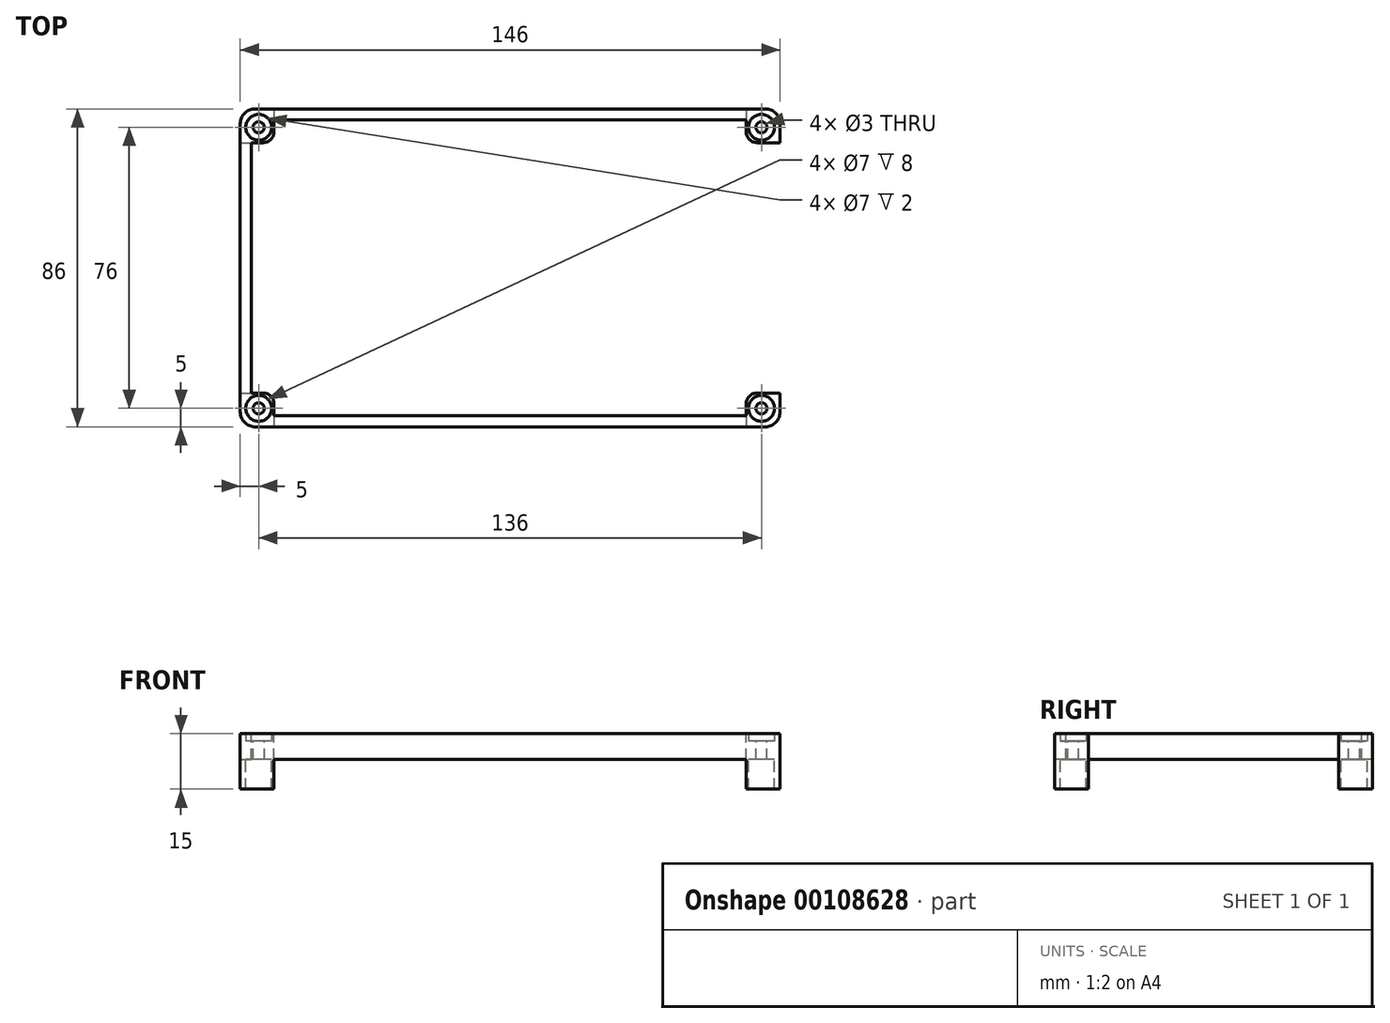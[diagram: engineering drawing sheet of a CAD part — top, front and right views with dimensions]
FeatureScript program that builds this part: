
annotation { "Feature Type Name" : "Feature", "Feature Type Description" : "" }
export const myFeature = defineFeature(function(context is Context, id is Id, definition is map)
    precondition{}
    {
        {
            var Q0;
            Q0=qCreatedBy(makeId("Top.planeOp"),FACE);
            var sketch = newSketch(context, id + "F0", { "sketchPlane" : qUnion([Q0])});
            skLineSegment(sketch, "E0.bottom", {"start": v(4, 0) * mm, "end": v(142, 0) * mm});
            skLineSegment(sketch, "E0.top", {"start": v(4, 86) * mm, "end": v(142, 86) * mm});
            skLineSegment(sketch, "E0.left", {"start": v(0, 4) * mm, "end": v(0, 82) * mm});
            skLineSegment(sketch, "E0.right", {"start": v(146, 4) * mm, "end": v(146, 82) * mm});
            skPoint(sketch, "E1", {"position": v(5, 5) * mm});
            skPoint(sketch, "E2", {"position": v(141, 5) * mm});
            skPoint(sketch, "E3", {"position": v(5, 81) * mm});
            skPoint(sketch, "E4", {"position": v(141, 81) * mm});
            skCircle(sketch, "E5", {"center": v(5, 5) * mm, "radius": 3 * mm, "construction": true});
            skCircle(sketch, "E6", {"center": v(5, 81) * mm, "radius": 3 * mm, "construction": true});
            skCircle(sketch, "E7", {"center": v(141, 81) * mm, "radius": 3 * mm, "construction": true});
            skCircle(sketch, "E8", {"center": v(141, 5) * mm, "radius": 3 * mm, "construction": true});
            skPoint(sketch, "E9", {"position": v(128.5, 7) * mm});
            skPoint(sketch, "E10", {"position": v(118.5, 7) * mm});
            skPoint(sketch, "E11", {"position": v(114.5, 7) * mm});
            skPoint(sketch, "E12", {"position": v(110.5, 7) * mm});
            skPoint(sketch, "E13", {"position": v(17.5, 79) * mm});
            skPoint(sketch, "E14", {"position": v(20.5, 79) * mm});
            skPoint(sketch, "E15", {"position": v(23.5, 79) * mm});
            skPoint(sketch, "E16", {"position": v(26.5, 79) * mm});
            skPoint(sketch, "E17", {"position": v(29.5, 79) * mm});
            skPoint(sketch, "E18", {"position": v(35, 79) * mm});
            skPoint(sketch, "E19", {"position": v(41, 79) * mm});
            skPoint(sketch, "E20", {"position": v(47, 79) * mm});
            skPoint(sketch, "E21", {"position": v(53, 79) * mm});
            skPoint(sketch, "E22", {"position": v(60, 79) * mm});
            skPoint(sketch, "E23", {"position": v(66, 79) * mm});
            skPoint(sketch, "E24", {"position": v(72, 79) * mm});
            skPoint(sketch, "E25", {"position": v(78, 79) * mm});
            skPoint(sketch, "E26", {"position": v(83.5, 79) * mm});
            skPoint(sketch, "E27", {"position": v(146, 10.15) * mm});
            skPoint(sketch, "E28", {"position": v(146, 75.85) * mm});
            skPoint(sketch, "E29", {"position": v(10.15, 0) * mm});
            skPoint(sketch, "E30", {"position": v(135.85, 0) * mm});
            skPoint(sketch, "E31", {"position": v(0, 75.85) * mm});
            skPoint(sketch, "E32", {"position": v(10.15, 86) * mm});
            skPoint(sketch, "E33", {"position": v(0, 10.15) * mm});
            skPoint(sketch, "E34", {"position": v(135.85, 86) * mm});
            skLineSegment(sketch, "E35.bottom", {"start": v(0, 86) * mm, "end": v(10.15, 86) * mm, "construction": true});
            skLineSegment(sketch, "E35.top", {"start": v(0, 75.85) * mm, "end": v(6.15, 75.85) * mm, "construction": true});
            skLineSegment(sketch, "E35.left", {"start": v(0, 86) * mm, "end": v(0, 75.85) * mm, "construction": true});
            skLineSegment(sketch, "E35.right", {"start": v(10.15, 86) * mm, "end": v(10.15, 79.85) * mm, "construction": true});
            skLineSegment(sketch, "E36.bottom", {"start": v(135.85, 86) * mm, "end": v(146, 86) * mm, "construction": true});
            skLineSegment(sketch, "E36.top", {"start": v(139.85, 75.85) * mm, "end": v(146, 75.85) * mm, "construction": true});
            skLineSegment(sketch, "E36.left", {"start": v(135.85, 86) * mm, "end": v(135.85, 79.85) * mm, "construction": true});
            skLineSegment(sketch, "E36.right", {"start": v(146, 86) * mm, "end": v(146, 75.85) * mm, "construction": true});
            skLineSegment(sketch, "E37.bottom", {"start": v(146, 10.15) * mm, "end": v(139.85, 10.15) * mm, "construction": true});
            skLineSegment(sketch, "E37.top", {"start": v(146, 0) * mm, "end": v(135.85, 0) * mm, "construction": true});
            skLineSegment(sketch, "E37.left", {"start": v(146, 10.15) * mm, "end": v(146, 0) * mm, "construction": true});
            skLineSegment(sketch, "E37.right", {"start": v(135.85, 6.15) * mm, "end": v(135.85, 0) * mm, "construction": true});
            skLineSegment(sketch, "E38.bottom", {"start": v(0, 10.15) * mm, "end": v(6.15, 10.15) * mm, "construction": true});
            skLineSegment(sketch, "E38.top", {"start": v(0, 0) * mm, "end": v(10.15, 0) * mm, "construction": true});
            skLineSegment(sketch, "E38.left", {"start": v(0, 10.15) * mm, "end": v(0, 0) * mm, "construction": true});
            skLineSegment(sketch, "E38.right", {"start": v(10.15, 6.15) * mm, "end": v(10.15, 0) * mm, "construction": true});
            skPoint(sketch, "E39.visualSharp", {"position": v(135.85, 75.85) * mm});
            skArc(sketch, "E39.filletArc", {"start": v(135.85, 79.85) * mm, "mid": v(137.02, 77.02) * mm, "end": v(139.85, 75.85) * mm, "construction": true});
            skPoint(sketch, "E40.visualSharp", {"position": v(135.85, 10.15) * mm});
            skArc(sketch, "E40.filletArc", {"start": v(139.85, 10.15) * mm, "mid": v(137.02, 8.98) * mm, "end": v(135.85, 6.15) * mm, "construction": true});
            skPoint(sketch, "E41.visualSharp", {"position": v(10.15, 10.15) * mm});
            skArc(sketch, "E41.filletArc", {"start": v(10.15, 6.15) * mm, "mid": v(8.98, 8.98) * mm, "end": v(6.15, 10.15) * mm, "construction": true});
            skPoint(sketch, "E42.visualSharp", {"position": v(10.15, 75.85) * mm});
            skArc(sketch, "E42.filletArc", {"start": v(6.15, 75.85) * mm, "mid": v(8.98, 77.02) * mm, "end": v(10.15, 79.85) * mm, "construction": true});
            skLineSegment(sketch, "E43.0", {"start": v(3, 83) * mm, "end": v(143, 83) * mm});
            skLineSegment(sketch, "E43.1", {"start": v(3, 3) * mm, "end": v(3, 83) * mm});
            skLineSegment(sketch, "E43.2", {"start": v(3, 3) * mm, "end": v(143, 3) * mm});
            skLineSegment(sketch, "E43.3", {"start": v(143, 3) * mm, "end": v(143, 83) * mm});
            skLineSegment(sketch, "E44.bottom", {"start": v(146, 14.15) * mm, "end": v(143, 14.15) * mm, "construction": true});
            skLineSegment(sketch, "E44.top", {"start": v(146, 20.15) * mm, "end": v(143, 20.15) * mm, "construction": true});
            skLineSegment(sketch, "E44.left", {"start": v(146, 14.15) * mm, "end": v(146, 20.15) * mm});
            skLineSegment(sketch, "E44.right", {"start": v(143, 14.15) * mm, "end": v(143, 20.15) * mm});
            skLineSegment(sketch, "E45.bottom", {"start": v(146, 24.15) * mm, "end": v(143, 24.15) * mm, "construction": true});
            skLineSegment(sketch, "E45.top", {"start": v(146, 30.15) * mm, "end": v(143, 30.15) * mm, "construction": true});
            skLineSegment(sketch, "E45.left", {"start": v(146, 24.15) * mm, "end": v(146, 30.15) * mm});
            skLineSegment(sketch, "E45.right", {"start": v(143, 24.15) * mm, "end": v(143, 30.15) * mm});
            skLineSegment(sketch, "E46.bottom", {"start": v(146, 71.85) * mm, "end": v(143, 71.85) * mm, "construction": true});
            skLineSegment(sketch, "E46.top", {"start": v(146, 65.85) * mm, "end": v(143, 65.85) * mm, "construction": true});
            skLineSegment(sketch, "E46.left", {"start": v(146, 71.85) * mm, "end": v(146, 65.85) * mm});
            skLineSegment(sketch, "E46.right", {"start": v(143, 71.85) * mm, "end": v(143, 65.85) * mm});
            skLineSegment(sketch, "E47.bottom", {"start": v(146, 61.85) * mm, "end": v(143, 61.85) * mm, "construction": true});
            skLineSegment(sketch, "E47.top", {"start": v(146, 55.85) * mm, "end": v(143, 55.85) * mm, "construction": true});
            skLineSegment(sketch, "E47.left", {"start": v(146, 61.85) * mm, "end": v(146, 55.85) * mm});
            skLineSegment(sketch, "E47.right", {"start": v(143, 61.85) * mm, "end": v(143, 55.85) * mm});
            skLineSegment(sketch, "E48.bottom", {"start": v(146, 51.85) * mm, "end": v(143, 51.85) * mm, "construction": true});
            skLineSegment(sketch, "E48.top", {"start": v(146, 45.85) * mm, "end": v(143, 45.85) * mm, "construction": true});
            skLineSegment(sketch, "E48.left", {"start": v(146, 51.85) * mm, "end": v(146, 45.85) * mm});
            skLineSegment(sketch, "E48.right", {"start": v(143, 51.85) * mm, "end": v(143, 45.85) * mm});
            skLineSegment(sketch, "E49.bottom", {"start": v(146, 41.85) * mm, "end": v(143, 41.85) * mm, "construction": true});
            skLineSegment(sketch, "E49.top", {"start": v(146, 35.85) * mm, "end": v(143, 35.85) * mm, "construction": true});
            skLineSegment(sketch, "E49.left", {"start": v(146, 41.85) * mm, "end": v(146, 35.85) * mm});
            skLineSegment(sketch, "E49.right", {"start": v(143, 41.85) * mm, "end": v(143, 35.85) * mm});
            skLineSegment(sketch, "E50.0", {"start": v(9.15, 6.15) * mm, "end": v(9.15, 0) * mm});
            skArc(sketch, "E50.1", {"start": v(9.15, 6.15) * mm, "mid": v(8.27, 8.27) * mm, "end": v(6.15, 9.15) * mm});
            skLineSegment(sketch, "E50.2", {"start": v(0, 9.15) * mm, "end": v(6.15, 9.15) * mm});
            skLineSegment(sketch, "E51.0", {"start": v(136.85, 6.15) * mm, "end": v(136.85, 0) * mm});
            skArc(sketch, "E51.1", {"start": v(139.85, 9.15) * mm, "mid": v(137.73, 8.27) * mm, "end": v(136.85, 6.15) * mm});
            skLineSegment(sketch, "E51.2", {"start": v(146, 9.15) * mm, "end": v(139.85, 9.15) * mm});
            skLineSegment(sketch, "E52.0", {"start": v(139.85, 76.85) * mm, "end": v(146, 76.85) * mm});
            skArc(sketch, "E52.1", {"start": v(136.85, 79.85) * mm, "mid": v(137.73, 77.73) * mm, "end": v(139.85, 76.85) * mm});
            skLineSegment(sketch, "E52.2", {"start": v(136.85, 86) * mm, "end": v(136.85, 79.85) * mm});
            skLineSegment(sketch, "E53.0", {"start": v(9.15, 86) * mm, "end": v(9.15, 79.85) * mm});
            skArc(sketch, "E53.1", {"start": v(6.15, 76.85) * mm, "mid": v(8.27, 77.73) * mm, "end": v(9.15, 79.85) * mm});
            skLineSegment(sketch, "E53.2", {"start": v(0, 76.85) * mm, "end": v(6.15, 76.85) * mm});
            skCircle(sketch, "E54.0", {"center": v(5, 5) * mm, "radius": 3.5 * mm});
            skCircle(sketch, "E55.0", {"center": v(141, 5) * mm, "radius": 3.5 * mm});
            skCircle(sketch, "E56.0", {"center": v(141, 81) * mm, "radius": 3.5 * mm});
            skCircle(sketch, "E57.0", {"center": v(5, 81) * mm, "radius": 3.5 * mm});
            skLineSegment(sketch, "E58.bottom", {"start": v(0, 14.15) * mm, "end": v(3, 14.15) * mm});
            skLineSegment(sketch, "E58.top", {"start": v(0, 20.15) * mm, "end": v(3, 20.15) * mm});
            skLineSegment(sketch, "E58.left", {"start": v(0, 14.15) * mm, "end": v(0, 20.15) * mm});
            skLineSegment(sketch, "E58.right", {"start": v(3, 14.15) * mm, "end": v(3, 20.15) * mm});
            skLineSegment(sketch, "E59.bottom", {"start": v(0, 24.15) * mm, "end": v(3, 24.15) * mm});
            skLineSegment(sketch, "E59.top", {"start": v(0, 30.15) * mm, "end": v(3, 30.15) * mm});
            skLineSegment(sketch, "E59.left", {"start": v(0, 24.15) * mm, "end": v(0, 30.15) * mm});
            skLineSegment(sketch, "E59.right", {"start": v(3, 24.15) * mm, "end": v(3, 30.15) * mm});
            skLineSegment(sketch, "E60.bottom", {"start": v(0, 35.85) * mm, "end": v(3, 35.85) * mm});
            skLineSegment(sketch, "E60.top", {"start": v(0, 41.85) * mm, "end": v(3, 41.85) * mm});
            skLineSegment(sketch, "E60.left", {"start": v(0, 35.85) * mm, "end": v(0, 41.85) * mm});
            skLineSegment(sketch, "E60.right", {"start": v(3, 35.85) * mm, "end": v(3, 41.85) * mm});
            skLineSegment(sketch, "E61.bottom", {"start": v(0, 45.85) * mm, "end": v(3, 45.85) * mm});
            skLineSegment(sketch, "E61.top", {"start": v(0, 51.85) * mm, "end": v(3, 51.85) * mm});
            skLineSegment(sketch, "E61.left", {"start": v(0, 45.85) * mm, "end": v(0, 51.85) * mm});
            skLineSegment(sketch, "E61.right", {"start": v(3, 45.85) * mm, "end": v(3, 51.85) * mm});
            skLineSegment(sketch, "E62.bottom", {"start": v(0, 55.85) * mm, "end": v(3, 55.85) * mm});
            skLineSegment(sketch, "E62.top", {"start": v(0, 61.85) * mm, "end": v(3, 61.85) * mm});
            skLineSegment(sketch, "E62.left", {"start": v(0, 55.85) * mm, "end": v(0, 61.85) * mm});
            skLineSegment(sketch, "E62.right", {"start": v(3, 55.85) * mm, "end": v(3, 61.85) * mm});
            skLineSegment(sketch, "E63.bottom", {"start": v(0, 65.85) * mm, "end": v(3, 65.85) * mm});
            skLineSegment(sketch, "E63.top", {"start": v(0, 71.85) * mm, "end": v(3, 71.85) * mm});
            skLineSegment(sketch, "E63.left", {"start": v(0, 65.85) * mm, "end": v(0, 71.85) * mm});
            skLineSegment(sketch, "E63.right", {"start": v(3, 65.85) * mm, "end": v(3, 71.85) * mm});
            skCircle(sketch, "E64", {"center": v(5, 5) * mm, "radius": 1.5 * mm});
            skCircle(sketch, "E65", {"center": v(5, 81) * mm, "radius": 1.5 * mm});
            skCircle(sketch, "E66", {"center": v(141, 81) * mm, "radius": 1.5 * mm});
            skCircle(sketch, "E67", {"center": v(141, 5) * mm, "radius": 1.5 * mm});
            skPoint(sketch, "E68.visualSharp", {"position": v(0, 0) * mm});
            skArc(sketch, "E68.filletArc", {"start": v(0, 4) * mm, "mid": v(1.17, 1.17) * mm, "end": v(4, 0) * mm});
            skPoint(sketch, "E69.visualSharp", {"position": v(146, 86) * mm});
            skArc(sketch, "E69.filletArc", {"start": v(146, 82) * mm, "mid": v(144.83, 84.83) * mm, "end": v(142, 86) * mm});
            skPoint(sketch, "E70.visualSharp", {"position": v(146, 0) * mm});
            skArc(sketch, "E70.filletArc", {"start": v(142, 0) * mm, "mid": v(144.83, 1.17) * mm, "end": v(146, 4) * mm});
            skPoint(sketch, "E71.visualSharp", {"position": v(0, 86) * mm});
            skArc(sketch, "E71.filletArc", {"start": v(4, 86) * mm, "mid": v(1.17, 84.83) * mm, "end": v(0, 82) * mm});
            skSolve(sketch);
        }
        {
            var Q0;
            {var subQ1=sQuery(id+"F0.wireOp",EDGE,"E38.top");Q0=makeQuery(id+"F0.imprint","IMPRINT",FACE,{"disambiguationData":[TD([[makeQuery(id+"F0.imprint","IMPRINT",EDGE,{"derivedFrom":subQ1}),1.0]])]});}
            var Q1;
            {var subQ0=sQuery(id+"F0.wireOp",EDGE,"E0.bottom");Q1=makeQuery(id+"F0.imprint","IMPRINT",FACE,{"disambiguationData":[TD([[makeQuery(id+"F0.imprint","IMPRINT",EDGE,{"derivedFrom":subQ0}),1.0]])]});}
            var Q2;
            {var subQ0=sQuery(id+"F0.wireOp",EDGE,"E0.left");Q2=makeQuery(id+"F0.imprint","IMPRINT",FACE,{"disambiguationData":[TD([[makeQuery(id+"F0.imprint","IMPRINT",EDGE,{"derivedFrom":subQ0}),-1.0]])]});}
            var Q3;
            {var subQ0=sQuery(id+"F0.wireOp",EDGE,"E41.filletArc");Q3=makeQuery(id+"F0.imprint","IMPRINT",FACE,{"disambiguationData":[TD([[makeQuery(id+"F0.imprint","IMPRINT",EDGE,{"derivedFrom":subQ0}),1.0]])]});}
            var Q4;
            {var subQ4=sQuery(id+"F0.wireOp",EDGE,"E35.bottom");Q4=makeQuery(id+"F0.imprint","IMPRINT",FACE,{"disambiguationData":[TD([[makeQuery(id+"F0.imprint","IMPRINT",EDGE,{"derivedFrom":subQ4}),-1.0]])]});}
            var Q5;
            {var subQ0=sQuery(id+"F0.wireOp",EDGE,"E42.filletArc");Q5=makeQuery(id+"F0.imprint","IMPRINT",FACE,{"disambiguationData":[TD([[makeQuery(id+"F0.imprint","IMPRINT",EDGE,{"derivedFrom":subQ0}),1.0]])]});}
            var Q6;
            {var subQ0=sQuery(id+"F0.wireOp",EDGE,"E0.top");Q6=makeQuery(id+"F0.imprint","IMPRINT",FACE,{"disambiguationData":[TD([[makeQuery(id+"F0.imprint","IMPRINT",EDGE,{"derivedFrom":subQ0}),-1.0]])]});}
            var Q7;
            {var subQ1=sQuery(id+"F0.wireOp",EDGE,"E36.bottom");Q7=makeQuery(id+"F0.imprint","IMPRINT",FACE,{"disambiguationData":[TD([[makeQuery(id+"F0.imprint","IMPRINT",EDGE,{"derivedFrom":subQ1}),-1.0]])]});}
            var Q8;
            {var subQ0=sQuery(id+"F0.wireOp",EDGE,"E39.filletArc");Q8=makeQuery(id+"F0.imprint","IMPRINT",FACE,{"disambiguationData":[TD([[makeQuery(id+"F0.imprint","IMPRINT",EDGE,{"derivedFrom":subQ0}),1.0]])]});}
            var Q9;
            {var subQ1=sQuery(id+"F0.wireOp",EDGE,"E37.top");Q9=makeQuery(id+"F0.imprint","IMPRINT",FACE,{"disambiguationData":[TD([[makeQuery(id+"F0.imprint","IMPRINT",EDGE,{"derivedFrom":subQ1}),-1.0]])]});}
            var Q10;
            {var subQ0=sQuery(id+"F0.wireOp",EDGE,"E40.filletArc");Q10=makeQuery(id+"F0.imprint","IMPRINT",FACE,{"disambiguationData":[TD([[makeQuery(id+"F0.imprint","IMPRINT",EDGE,{"derivedFrom":subQ0}),1.0]])]});}
            var Q11;
            {var subQ3=sQuery(id+"F0.wireOp",EDGE,"E44.bottom");Q11=makeQuery(id+"F0.imprint","IMPRINT",FACE,{"disambiguationData":[TD([[makeQuery(id+"F0.imprint","IMPRINT",EDGE,{"derivedFrom":subQ3}),1.0]])]});}
            var Q12;
            Q12=makeQuery(id+"F0.imprint","IMPRINT",FACE,{"disambiguationData":[TD([[makeQuery(id+"F0.imprint","IMPRINT",EDGE,{"derivedFrom":sQuery(id+"F0.wireOp",EDGE,"E44.bottom")}),-1.0]])]});
            var Q13;
            {var subQ0=sQuery(id+"F0.wireOp",EDGE,"E44.top");Q13=makeQuery(id+"F0.imprint","IMPRINT",FACE,{"disambiguationData":[TD([[makeQuery(id+"F0.imprint","IMPRINT",EDGE,{"derivedFrom":subQ0}),-1.0]])]});}
            var Q14;
            Q14=makeQuery(id+"F0.imprint","IMPRINT",FACE,{"disambiguationData":[TD([[makeQuery(id+"F0.imprint","IMPRINT",EDGE,{"derivedFrom":sQuery(id+"F0.wireOp",EDGE,"E45.bottom")}),-1.0]])]});
            var Q15;
            {var subQ0=sQuery(id+"F0.wireOp",EDGE,"E45.top");Q15=makeQuery(id+"F0.imprint","IMPRINT",FACE,{"disambiguationData":[TD([[makeQuery(id+"F0.imprint","IMPRINT",EDGE,{"derivedFrom":subQ0}),-1.0]])]});}
            var Q16;
            Q16=makeQuery(id+"F0.imprint","IMPRINT",FACE,{"disambiguationData":[TD([[makeQuery(id+"F0.imprint","IMPRINT",EDGE,{"derivedFrom":sQuery(id+"F0.wireOp",EDGE,"E49.bottom")}),1.0]])]});
            var Q17;
            {var subQ0=sQuery(id+"F0.wireOp",EDGE,"E48.top");Q17=makeQuery(id+"F0.imprint","IMPRINT",FACE,{"disambiguationData":[TD([[makeQuery(id+"F0.imprint","IMPRINT",EDGE,{"derivedFrom":subQ0}),1.0]])]});}
            var Q18;
            Q18=makeQuery(id+"F0.imprint","IMPRINT",FACE,{"disambiguationData":[TD([[makeQuery(id+"F0.imprint","IMPRINT",EDGE,{"derivedFrom":sQuery(id+"F0.wireOp",EDGE,"E48.bottom")}),1.0]])]});
            var Q19;
            {var subQ0=sQuery(id+"F0.wireOp",EDGE,"E47.top");Q19=makeQuery(id+"F0.imprint","IMPRINT",FACE,{"disambiguationData":[TD([[makeQuery(id+"F0.imprint","IMPRINT",EDGE,{"derivedFrom":subQ0}),1.0]])]});}
            var Q20;
            Q20=makeQuery(id+"F0.imprint","IMPRINT",FACE,{"disambiguationData":[TD([[makeQuery(id+"F0.imprint","IMPRINT",EDGE,{"derivedFrom":sQuery(id+"F0.wireOp",EDGE,"E47.bottom")}),1.0]])]});
            var Q21;
            {var subQ0=sQuery(id+"F0.wireOp",EDGE,"E46.top");Q21=makeQuery(id+"F0.imprint","IMPRINT",FACE,{"disambiguationData":[TD([[makeQuery(id+"F0.imprint","IMPRINT",EDGE,{"derivedFrom":subQ0}),1.0]])]});}
            var Q22;
            Q22=makeQuery(id+"F0.imprint","IMPRINT",FACE,{"disambiguationData":[TD([[makeQuery(id+"F0.imprint","IMPRINT",EDGE,{"derivedFrom":sQuery(id+"F0.wireOp",EDGE,"E46.bottom")}),1.0]])]});
            var Q23;
            {var subQ3=sQuery(id+"F0.wireOp",EDGE,"E46.bottom");Q23=makeQuery(id+"F0.imprint","IMPRINT",FACE,{"disambiguationData":[TD([[makeQuery(id+"F0.imprint","IMPRINT",EDGE,{"derivedFrom":subQ3}),-1.0]])]});}
            var Q24;
            {var subQ0=sQuery(id+"F0.wireOp",EDGE,"E43.1");var subQ1=sQuery(id+"F0.wireOp",EDGE,"E5");var subQ2=makeQuery(id+"F0.imprint","INTERSECT",VERTEX,{"derivedFrom":[subQ1,subQ0]});Q24=makeQuery(id+"F0.imprint","IMPRINT",FACE,{"disambiguationData":[TD([[makeQuery(id+"F0.imprint","IMPRINT",EDGE,{"disambiguationData":[TD([[subQ2,-1.0]])],"derivedFrom":subQ1}),-1.0]])]});}
            var Q25;
            {var subQ0=sQuery(id+"F0.wireOp",EDGE,"E50.1");Q25=makeQuery(id+"F0.imprint","IMPRINT",FACE,{"disambiguationData":[TD([[makeQuery(id+"F0.imprint","IMPRINT",EDGE,{"derivedFrom":subQ0}),1.0]])]});}
            var Q26;
            {var subQ0=sQuery(id+"F0.wireOp",EDGE,"E43.0");var subQ1=sQuery(id+"F0.wireOp",EDGE,"E6");var subQ2=makeQuery(id+"F0.imprint","INTERSECT",VERTEX,{"derivedFrom":[subQ1,subQ0]});Q26=makeQuery(id+"F0.imprint","IMPRINT",FACE,{"disambiguationData":[TD([[makeQuery(id+"F0.imprint","IMPRINT",EDGE,{"disambiguationData":[TD([[subQ2,-1.0]])],"derivedFrom":subQ1}),-1.0]])]});}
            var Q27;
            {var subQ0=sQuery(id+"F0.wireOp",EDGE,"E53.1");Q27=makeQuery(id+"F0.imprint","IMPRINT",FACE,{"disambiguationData":[TD([[makeQuery(id+"F0.imprint","IMPRINT",EDGE,{"derivedFrom":subQ0}),1.0]])]});}
            var Q28;
            {var subQ0=sQuery(id+"F0.wireOp",EDGE,"E43.0");var subQ1=sQuery(id+"F0.wireOp",EDGE,"E7");var subQ2=makeQuery(id+"F0.imprint","INTERSECT",VERTEX,{"derivedFrom":[subQ1,subQ0]});Q28=makeQuery(id+"F0.imprint","IMPRINT",FACE,{"disambiguationData":[TD([[makeQuery(id+"F0.imprint","IMPRINT",EDGE,{"disambiguationData":[TD([[subQ2,1.0]])],"derivedFrom":subQ1}),-1.0]])]});}
            var Q29;
            {var subQ5=sQuery(id+"F0.wireOp",EDGE,"E52.1");Q29=makeQuery(id+"F0.imprint","IMPRINT",FACE,{"disambiguationData":[TD([[makeQuery(id+"F0.imprint","IMPRINT",EDGE,{"derivedFrom":subQ5}),1.0]])]});}
            var Q30;
            {var subQ0=sQuery(id+"F0.wireOp",EDGE,"E43.2");var subQ1=sQuery(id+"F0.wireOp",EDGE,"E8");var subQ2=makeQuery(id+"F0.imprint","INTERSECT",VERTEX,{"derivedFrom":[subQ1,subQ0]});Q30=makeQuery(id+"F0.imprint","IMPRINT",FACE,{"disambiguationData":[TD([[makeQuery(id+"F0.imprint","IMPRINT",EDGE,{"disambiguationData":[TD([[subQ2,-1.0]])],"derivedFrom":subQ1}),-1.0]])]});}
            var Q31;
            {var subQ0=sQuery(id+"F0.wireOp",EDGE,"E51.1");Q31=makeQuery(id+"F0.imprint","IMPRINT",FACE,{"disambiguationData":[TD([[makeQuery(id+"F0.imprint","IMPRINT",EDGE,{"derivedFrom":subQ0}),1.0]])]});}
            var Q32;
            {var subQ6=sQuery(id+"F0.wireOp",EDGE,"E38.left");var subQ11=sQuery(id+"F0.wireOp",EDGE,"E38.top");var subQ13=makeQuery(id+"F0.imprint","INTERSECT",VERTEX,{"derivedFrom":[subQ11,subQ6]});Q32=makeQuery(id+"F0.imprint","IMPRINT",FACE,{"disambiguationData":[TD([[makeQuery(id+"F0.imprint","IMPRINT",EDGE,{"disambiguationData":[TD([[subQ13,-1.0]])],"derivedFrom":subQ11}),1.0]])]});}
            var Q33;
            {var subQ5=sQuery(id+"F0.wireOp",EDGE,"E37.left");var subQ6=sQuery(id+"F0.wireOp",EDGE,"E37.top");var subQ7=makeQuery(id+"F0.imprint","INTERSECT",VERTEX,{"derivedFrom":[subQ6,subQ5]});Q33=makeQuery(id+"F0.imprint","IMPRINT",FACE,{"disambiguationData":[TD([[makeQuery(id+"F0.imprint","IMPRINT",EDGE,{"disambiguationData":[TD([[subQ7,-1.0]])],"derivedFrom":subQ6}),-1.0]])]});}
            var Q34;
            {var subQ5=sQuery(id+"F0.wireOp",EDGE,"E36.right");var subQ6=sQuery(id+"F0.wireOp",EDGE,"E36.bottom");var subQ7=makeQuery(id+"F0.imprint","INTERSECT",VERTEX,{"derivedFrom":[subQ6,subQ5]});Q34=makeQuery(id+"F0.imprint","IMPRINT",FACE,{"disambiguationData":[TD([[makeQuery(id+"F0.imprint","IMPRINT",EDGE,{"disambiguationData":[TD([[subQ7,1.0]])],"derivedFrom":subQ6}),-1.0]])]});}
            var Q35;
            {var subQ9=sQuery(id+"F0.wireOp",EDGE,"E35.left");var subQ10=sQuery(id+"F0.wireOp",EDGE,"E35.bottom");var subQ11=makeQuery(id+"F0.imprint","INTERSECT",VERTEX,{"derivedFrom":[subQ10,subQ9]});Q35=makeQuery(id+"F0.imprint","IMPRINT",FACE,{"disambiguationData":[TD([[makeQuery(id+"F0.imprint","IMPRINT",EDGE,{"disambiguationData":[TD([[subQ11,-1.0]])],"derivedFrom":subQ10}),-1.0]])]});}
            var Q36;
            {var subQ5=sQuery(id+"F0.wireOp",EDGE,"E58.bottom");Q36=makeQuery(id+"F0.imprint","IMPRINT",FACE,{"disambiguationData":[TD([[makeQuery(id+"F0.imprint","IMPRINT",EDGE,{"derivedFrom":subQ5}),-1.0]])]});}
            var Q37;
            Q37=makeQuery(id+"F0.imprint","IMPRINT",FACE,{"disambiguationData":[TD([[makeQuery(id+"F0.imprint","IMPRINT",EDGE,{"derivedFrom":sQuery(id+"F0.wireOp",EDGE,"E58.bottom")}),1.0]])]});
            var Q38;
            Q38=makeQuery(id+"F0.imprint","IMPRINT",FACE,{"disambiguationData":[TD([[makeQuery(id+"F0.imprint","IMPRINT",EDGE,{"derivedFrom":sQuery(id+"F0.wireOp",EDGE,"E59.bottom")}),1.0]])]});
            var Q39;
            Q39=makeQuery(id+"F0.imprint","IMPRINT",FACE,{"disambiguationData":[TD([[makeQuery(id+"F0.imprint","IMPRINT",EDGE,{"derivedFrom":sQuery(id+"F0.wireOp",EDGE,"E60.bottom")}),1.0]])]});
            var Q40;
            Q40=makeQuery(id+"F0.imprint","IMPRINT",FACE,{"disambiguationData":[TD([[makeQuery(id+"F0.imprint","IMPRINT",EDGE,{"derivedFrom":sQuery(id+"F0.wireOp",EDGE,"E61.bottom")}),1.0]])]});
            var Q41;
            Q41=makeQuery(id+"F0.imprint","IMPRINT",FACE,{"disambiguationData":[TD([[makeQuery(id+"F0.imprint","IMPRINT",EDGE,{"derivedFrom":sQuery(id+"F0.wireOp",EDGE,"E62.bottom")}),1.0]])]});
            var Q42;
            Q42=makeQuery(id+"F0.imprint","IMPRINT",FACE,{"disambiguationData":[TD([[makeQuery(id+"F0.imprint","IMPRINT",EDGE,{"derivedFrom":sQuery(id+"F0.wireOp",EDGE,"E63.bottom")}),1.0]])]});
            var Q43;
            {var subQ0=sQuery(id+"F0.wireOp",EDGE,"E63.top");Q43=makeQuery(id+"F0.imprint","IMPRINT",FACE,{"disambiguationData":[TD([[makeQuery(id+"F0.imprint","IMPRINT",EDGE,{"derivedFrom":subQ0}),1.0]])]});}
            var Q44;
            {var subQ4=sQuery(id+"F0.wireOp",EDGE,"E44.left");Q44=makeQuery(id+"F0.imprint","IMPRINT",FACE,{"disambiguationData":[TD([[makeQuery(id+"F0.imprint","IMPRINT",EDGE,{"derivedFrom":subQ4}),1.0]])]});}
            var Q45;
            {var subQ0=sQuery(id+"F0.wireOp",EDGE,"E43.2");var subQ1=sQuery(id+"F0.wireOp",EDGE,"E43.1");var subQ2=makeQuery(id+"F0.imprint","INTERSECT",VERTEX,{"derivedFrom":[subQ1,subQ0]});Q45=makeQuery(id+"F0.imprint","IMPRINT",FACE,{"disambiguationData":[TD([[makeQuery(id+"F0.imprint","IMPRINT",EDGE,{"disambiguationData":[TD([[subQ2,-1.0]])],"derivedFrom":subQ1}),1.0]])]});}
            var Q46;
            Q46=makeQuery(id+"F0.imprint","IMPRINT",FACE,{"disambiguationData":[TD([[makeQuery(id+"F0.imprint","IMPRINT",EDGE,{"derivedFrom":sQuery(id+"F0.wireOp",EDGE,"E64")}),-1.0]])]});
            var Q47;
            {var subQ0=sQuery(id+"F0.wireOp",EDGE,"E43.1");var subQ1=sQuery(id+"F0.wireOp",EDGE,"E43.0");var subQ2=makeQuery(id+"F0.imprint","INTERSECT",VERTEX,{"derivedFrom":[subQ1,subQ0]});Q47=makeQuery(id+"F0.imprint","IMPRINT",FACE,{"disambiguationData":[TD([[makeQuery(id+"F0.imprint","IMPRINT",EDGE,{"disambiguationData":[TD([[subQ2,-1.0]])],"derivedFrom":subQ1}),1.0]])]});}
            var Q48;
            Q48=makeQuery(id+"F0.imprint","IMPRINT",FACE,{"disambiguationData":[TD([[makeQuery(id+"F0.imprint","IMPRINT",EDGE,{"derivedFrom":sQuery(id+"F0.wireOp",EDGE,"E65")}),-1.0]])]});
            var Q49;
            {var subQ0=sQuery(id+"F0.wireOp",EDGE,"E43.3");var subQ1=sQuery(id+"F0.wireOp",EDGE,"E43.0");var subQ2=makeQuery(id+"F0.imprint","INTERSECT",VERTEX,{"derivedFrom":[subQ1,subQ0]});Q49=makeQuery(id+"F0.imprint","IMPRINT",FACE,{"disambiguationData":[TD([[makeQuery(id+"F0.imprint","IMPRINT",EDGE,{"disambiguationData":[TD([[subQ2,1.0]])],"derivedFrom":subQ1}),1.0]])]});}
            var Q50;
            Q50=makeQuery(id+"F0.imprint","IMPRINT",FACE,{"disambiguationData":[TD([[makeQuery(id+"F0.imprint","IMPRINT",EDGE,{"derivedFrom":sQuery(id+"F0.wireOp",EDGE,"E66")}),-1.0]])]});
            var Q51;
            Q51=makeQuery(id+"F0.imprint","IMPRINT",FACE,{"disambiguationData":[TD([[makeQuery(id+"F0.imprint","IMPRINT",EDGE,{"derivedFrom":sQuery(id+"F0.wireOp",EDGE,"E67")}),-1.0]])]});
            var Q52;
            {var subQ0=sQuery(id+"F0.wireOp",EDGE,"E43.3");var subQ1=sQuery(id+"F0.wireOp",EDGE,"E43.2");var subQ2=makeQuery(id+"F0.imprint","INTERSECT",VERTEX,{"derivedFrom":[subQ1,subQ0]});Q52=makeQuery(id+"F0.imprint","IMPRINT",FACE,{"disambiguationData":[TD([[makeQuery(id+"F0.imprint","IMPRINT",EDGE,{"disambiguationData":[TD([[subQ2,1.0]])],"derivedFrom":subQ1}),-1.0]])]});}
            var Q53;
            {var subQ11=sQuery(id+"F0.wireOp",EDGE,"E68.filletArc");Q53=makeQuery(id+"F0.imprint","IMPRINT",FACE,{"disambiguationData":[TD([[makeQuery(id+"F0.imprint","IMPRINT",EDGE,{"derivedFrom":subQ11}),1.0]])]});}
            var Q54;
            {var subQ5=sQuery(id+"F0.wireOp",EDGE,"E71.filletArc");Q54=makeQuery(id+"F0.imprint","IMPRINT",FACE,{"disambiguationData":[TD([[makeQuery(id+"F0.imprint","IMPRINT",EDGE,{"derivedFrom":subQ5}),1.0]])]});}
            var Q55;
            {var subQ9=sQuery(id+"F0.wireOp",EDGE,"E69.filletArc");Q55=makeQuery(id+"F0.imprint","IMPRINT",FACE,{"disambiguationData":[TD([[makeQuery(id+"F0.imprint","IMPRINT",EDGE,{"derivedFrom":subQ9}),1.0]])]});}
            var Q56;
            {var subQ9=sQuery(id+"F0.wireOp",EDGE,"E70.filletArc");Q56=makeQuery(id+"F0.imprint","IMPRINT",FACE,{"disambiguationData":[TD([[makeQuery(id+"F0.imprint","IMPRINT",EDGE,{"derivedFrom":subQ9}),1.0]])]});}
            extrude(context, id + "F1", {"entities" : qUnion([Q0, Q1, Q2, Q3, Q4, Q5, Q6, Q7, Q8, Q9, Q10, Q11, Q12, Q13, Q14, Q15, Q16, Q17, Q18, Q19, Q20, Q21, Q22, Q23, Q24, Q25, Q26, Q27, Q28, Q29, Q30, Q31, Q32, Q33, Q34, Q35, Q36, Q37, Q38, Q39, Q40, Q41, Q42, Q43, Q44, Q45, Q46, Q47, Q48, Q49, Q50, Q51, Q52, Q53, Q54, Q55, Q56]), "oppositeDirection" : true, "depth" : 2.5 * mm});
        }
        {
            var Q0;
            {var subQ0=sQuery(id+"F0.wireOp",EDGE,"E0.bottom");Q0=makeQuery(id+"F0.imprint","IMPRINT",FACE,{"disambiguationData":[TD([[makeQuery(id+"F0.imprint","IMPRINT",EDGE,{"derivedFrom":subQ0}),1.0]])]});}
            var Q1;
            {var subQ0=sQuery(id+"F0.wireOp",EDGE,"E0.left");Q1=makeQuery(id+"F0.imprint","IMPRINT",FACE,{"disambiguationData":[TD([[makeQuery(id+"F0.imprint","IMPRINT",EDGE,{"derivedFrom":subQ0}),-1.0]])]});}
            var Q2;
            {var subQ0=sQuery(id+"F0.wireOp",EDGE,"E0.top");Q2=makeQuery(id+"F0.imprint","IMPRINT",FACE,{"disambiguationData":[TD([[makeQuery(id+"F0.imprint","IMPRINT",EDGE,{"derivedFrom":subQ0}),-1.0]])]});}
            var Q3;
            {var subQ3=sQuery(id+"F0.wireOp",EDGE,"E46.bottom");Q3=makeQuery(id+"F0.imprint","IMPRINT",FACE,{"disambiguationData":[TD([[makeQuery(id+"F0.imprint","IMPRINT",EDGE,{"derivedFrom":subQ3}),-1.0]])]});}
            var Q4;
            {var subQ0=sQuery(id+"F0.wireOp",EDGE,"E46.top");Q4=makeQuery(id+"F0.imprint","IMPRINT",FACE,{"disambiguationData":[TD([[makeQuery(id+"F0.imprint","IMPRINT",EDGE,{"derivedFrom":subQ0}),1.0]])]});}
            var Q5;
            {var subQ0=sQuery(id+"F0.wireOp",EDGE,"E47.top");Q5=makeQuery(id+"F0.imprint","IMPRINT",FACE,{"disambiguationData":[TD([[makeQuery(id+"F0.imprint","IMPRINT",EDGE,{"derivedFrom":subQ0}),1.0]])]});}
            var Q6;
            {var subQ0=sQuery(id+"F0.wireOp",EDGE,"E48.top");Q6=makeQuery(id+"F0.imprint","IMPRINT",FACE,{"disambiguationData":[TD([[makeQuery(id+"F0.imprint","IMPRINT",EDGE,{"derivedFrom":subQ0}),1.0]])]});}
            var Q7;
            {var subQ0=sQuery(id+"F0.wireOp",EDGE,"E45.top");Q7=makeQuery(id+"F0.imprint","IMPRINT",FACE,{"disambiguationData":[TD([[makeQuery(id+"F0.imprint","IMPRINT",EDGE,{"derivedFrom":subQ0}),-1.0]])]});}
            var Q8;
            {var subQ0=sQuery(id+"F0.wireOp",EDGE,"E44.top");Q8=makeQuery(id+"F0.imprint","IMPRINT",FACE,{"disambiguationData":[TD([[makeQuery(id+"F0.imprint","IMPRINT",EDGE,{"derivedFrom":subQ0}),-1.0]])]});}
            var Q9;
            {var subQ3=sQuery(id+"F0.wireOp",EDGE,"E44.bottom");Q9=makeQuery(id+"F0.imprint","IMPRINT",FACE,{"disambiguationData":[TD([[makeQuery(id+"F0.imprint","IMPRINT",EDGE,{"derivedFrom":subQ3}),1.0]])]});}
            var Q10;
            {var subQ4=sQuery(id+"F0.wireOp",EDGE,"E35.bottom");Q10=makeQuery(id+"F0.imprint","IMPRINT",FACE,{"disambiguationData":[TD([[makeQuery(id+"F0.imprint","IMPRINT",EDGE,{"derivedFrom":subQ4}),-1.0]])]});}
            var Q11;
            {var subQ0=sQuery(id+"F0.wireOp",EDGE,"E42.filletArc");Q11=makeQuery(id+"F0.imprint","IMPRINT",FACE,{"disambiguationData":[TD([[makeQuery(id+"F0.imprint","IMPRINT",EDGE,{"derivedFrom":subQ0}),1.0]])]});}
            var Q12;
            {var subQ1=sQuery(id+"F0.wireOp",EDGE,"E38.top");Q12=makeQuery(id+"F0.imprint","IMPRINT",FACE,{"disambiguationData":[TD([[makeQuery(id+"F0.imprint","IMPRINT",EDGE,{"derivedFrom":subQ1}),1.0]])]});}
            var Q13;
            {var subQ0=sQuery(id+"F0.wireOp",EDGE,"E41.filletArc");Q13=makeQuery(id+"F0.imprint","IMPRINT",FACE,{"disambiguationData":[TD([[makeQuery(id+"F0.imprint","IMPRINT",EDGE,{"derivedFrom":subQ0}),1.0]])]});}
            var Q14;
            {var subQ1=sQuery(id+"F0.wireOp",EDGE,"E37.top");Q14=makeQuery(id+"F0.imprint","IMPRINT",FACE,{"disambiguationData":[TD([[makeQuery(id+"F0.imprint","IMPRINT",EDGE,{"derivedFrom":subQ1}),-1.0]])]});}
            var Q15;
            {var subQ1=sQuery(id+"F0.wireOp",EDGE,"E36.bottom");Q15=makeQuery(id+"F0.imprint","IMPRINT",FACE,{"disambiguationData":[TD([[makeQuery(id+"F0.imprint","IMPRINT",EDGE,{"derivedFrom":subQ1}),-1.0]])]});}
            var Q16;
            {var subQ0=sQuery(id+"F0.wireOp",EDGE,"E39.filletArc");Q16=makeQuery(id+"F0.imprint","IMPRINT",FACE,{"disambiguationData":[TD([[makeQuery(id+"F0.imprint","IMPRINT",EDGE,{"derivedFrom":subQ0}),1.0]])]});}
            var Q17;
            {var subQ0=sQuery(id+"F0.wireOp",EDGE,"E40.filletArc");Q17=makeQuery(id+"F0.imprint","IMPRINT",FACE,{"disambiguationData":[TD([[makeQuery(id+"F0.imprint","IMPRINT",EDGE,{"derivedFrom":subQ0}),1.0]])]});}
            var Q18;
            {var subQ5=sQuery(id+"F0.wireOp",EDGE,"E58.bottom");Q18=makeQuery(id+"F0.imprint","IMPRINT",FACE,{"disambiguationData":[TD([[makeQuery(id+"F0.imprint","IMPRINT",EDGE,{"derivedFrom":subQ5}),-1.0]])]});}
            var Q19;
            {var subQ0=sQuery(id+"F0.wireOp",EDGE,"E63.top");Q19=makeQuery(id+"F0.imprint","IMPRINT",FACE,{"disambiguationData":[TD([[makeQuery(id+"F0.imprint","IMPRINT",EDGE,{"derivedFrom":subQ0}),1.0]])]});}
            var Q20;
            {var subQ4=sQuery(id+"F0.wireOp",EDGE,"E44.left");Q20=makeQuery(id+"F0.imprint","IMPRINT",FACE,{"disambiguationData":[TD([[makeQuery(id+"F0.imprint","IMPRINT",EDGE,{"derivedFrom":subQ4}),1.0]])]});}
            var Q21;
            {var subQ0=sQuery(id+"F0.wireOp",EDGE,"E43.2");var subQ1=sQuery(id+"F0.wireOp",EDGE,"E43.1");var subQ2=makeQuery(id+"F0.imprint","INTERSECT",VERTEX,{"derivedFrom":[subQ1,subQ0]});Q21=makeQuery(id+"F0.imprint","IMPRINT",FACE,{"disambiguationData":[TD([[makeQuery(id+"F0.imprint","IMPRINT",EDGE,{"disambiguationData":[TD([[subQ2,-1.0]])],"derivedFrom":subQ1}),1.0]])]});}
            var Q22;
            Q22=makeQuery(id+"F0.imprint","IMPRINT",FACE,{"disambiguationData":[TD([[makeQuery(id+"F0.imprint","IMPRINT",EDGE,{"derivedFrom":sQuery(id+"F0.wireOp",EDGE,"E64")}),-1.0]])]});
            var Q23;
            Q23=makeQuery(id+"F0.imprint","IMPRINT",FACE,{"disambiguationData":[TD([[makeQuery(id+"F0.imprint","IMPRINT",EDGE,{"derivedFrom":sQuery(id+"F0.wireOp",EDGE,"E67")}),-1.0]])]});
            var Q24;
            {var subQ0=sQuery(id+"F0.wireOp",EDGE,"E43.3");var subQ1=sQuery(id+"F0.wireOp",EDGE,"E43.2");var subQ2=makeQuery(id+"F0.imprint","INTERSECT",VERTEX,{"derivedFrom":[subQ1,subQ0]});Q24=makeQuery(id+"F0.imprint","IMPRINT",FACE,{"disambiguationData":[TD([[makeQuery(id+"F0.imprint","IMPRINT",EDGE,{"disambiguationData":[TD([[subQ2,1.0]])],"derivedFrom":subQ1}),-1.0]])]});}
            var Q25;
            {var subQ0=sQuery(id+"F0.wireOp",EDGE,"E43.3");var subQ1=sQuery(id+"F0.wireOp",EDGE,"E43.0");var subQ2=makeQuery(id+"F0.imprint","INTERSECT",VERTEX,{"derivedFrom":[subQ1,subQ0]});Q25=makeQuery(id+"F0.imprint","IMPRINT",FACE,{"disambiguationData":[TD([[makeQuery(id+"F0.imprint","IMPRINT",EDGE,{"disambiguationData":[TD([[subQ2,1.0]])],"derivedFrom":subQ1}),1.0]])]});}
            var Q26;
            Q26=makeQuery(id+"F0.imprint","IMPRINT",FACE,{"disambiguationData":[TD([[makeQuery(id+"F0.imprint","IMPRINT",EDGE,{"derivedFrom":sQuery(id+"F0.wireOp",EDGE,"E66")}),-1.0]])]});
            var Q27;
            Q27=makeQuery(id+"F0.imprint","IMPRINT",FACE,{"disambiguationData":[TD([[makeQuery(id+"F0.imprint","IMPRINT",EDGE,{"derivedFrom":sQuery(id+"F0.wireOp",EDGE,"E65")}),-1.0]])]});
            var Q28;
            {var subQ0=sQuery(id+"F0.wireOp",EDGE,"E43.1");var subQ1=sQuery(id+"F0.wireOp",EDGE,"E43.0");var subQ2=makeQuery(id+"F0.imprint","INTERSECT",VERTEX,{"derivedFrom":[subQ1,subQ0]});Q28=makeQuery(id+"F0.imprint","IMPRINT",FACE,{"disambiguationData":[TD([[makeQuery(id+"F0.imprint","IMPRINT",EDGE,{"disambiguationData":[TD([[subQ2,-1.0]])],"derivedFrom":subQ1}),1.0]])]});}
            var Q29;
            Q29=makeQuery(id+"F1.opExtrude","CAP_FACE",FACE,{"disambiguationData":[OSD([sQuery(id+"F0.wireOp",EDGE,"E0.bottom"),sQuery(id+"F0.wireOp",EDGE,"E0.top"),sQuery(id+"F0.wireOp",EDGE,"E0.left"),sQuery(id+"F0.wireOp",EDGE,"E0.right"),sQuery(id+"F0.wireOp",EDGE,"E5"),sQuery(id+"F0.wireOp",EDGE,"E6"),sQuery(id+"F0.wireOp",EDGE,"E7"),sQuery(id+"F0.wireOp",EDGE,"E8"),sQuery(id+"F0.wireOp",EDGE,"E35.bottom"),sQuery(id+"F0.wireOp",EDGE,"E35.top"),sQuery(id+"F0.wireOp",EDGE,"E35.left"),sQuery(id+"F0.wireOp",EDGE,"E35.right"),sQuery(id+"F0.wireOp",EDGE,"E36.bottom"),sQuery(id+"F0.wireOp",EDGE,"E36.top"),sQuery(id+"F0.wireOp",EDGE,"E36.left"),sQuery(id+"F0.wireOp",EDGE,"E36.right"),sQuery(id+"F0.wireOp",EDGE,"E37.bottom"),sQuery(id+"F0.wireOp",EDGE,"E37.top"),sQuery(id+"F0.wireOp",EDGE,"E37.left"),sQuery(id+"F0.wireOp",EDGE,"E37.right"),sQuery(id+"F0.wireOp",EDGE,"E38.bottom"),sQuery(id+"F0.wireOp",EDGE,"E38.top"),sQuery(id+"F0.wireOp",EDGE,"E38.left"),sQuery(id+"F0.wireOp",EDGE,"E38.right"),sQuery(id+"F0.wireOp",EDGE,"E39.filletArc"),sQuery(id+"F0.wireOp",EDGE,"E40.filletArc"),sQuery(id+"F0.wireOp",EDGE,"E41.filletArc"),sQuery(id+"F0.wireOp",EDGE,"E42.filletArc"),sQuery(id+"F0.wireOp",EDGE,"E43.0"),sQuery(id+"F0.wireOp",EDGE,"E43.1"),sQuery(id+"F0.wireOp",EDGE,"E43.2"),sQuery(id+"F0.wireOp",EDGE,"E43.3"),sQuery(id+"F0.wireOp",EDGE,"E44.left"),sQuery(id+"F0.wireOp",EDGE,"E44.right"),sQuery(id+"F0.wireOp",EDGE,"E45.left"),sQuery(id+"F0.wireOp",EDGE,"E45.right"),sQuery(id+"F0.wireOp",EDGE,"E46.left"),sQuery(id+"F0.wireOp",EDGE,"E46.right"),sQuery(id+"F0.wireOp",EDGE,"E47.left"),sQuery(id+"F0.wireOp",EDGE,"E47.right"),sQuery(id+"F0.wireOp",EDGE,"E48.left"),sQuery(id+"F0.wireOp",EDGE,"E48.right"),sQuery(id+"F0.wireOp",EDGE,"E49.left"),sQuery(id+"F0.wireOp",EDGE,"E49.right")])],"isStart":false});
            var Q30;
            Q30=makeQuery(id+"F1.opExtrude","SWEPT_BODY",BODY,{"disambiguationData":[OSD([sQuery(id+"F0.wireOp",EDGE,"E0.bottom"),sQuery(id+"F0.wireOp",EDGE,"E0.top"),sQuery(id+"F0.wireOp",EDGE,"E0.left"),sQuery(id+"F0.wireOp",EDGE,"E0.right"),sQuery(id+"F0.wireOp",EDGE,"E5"),sQuery(id+"F0.wireOp",EDGE,"E6"),sQuery(id+"F0.wireOp",EDGE,"E7"),sQuery(id+"F0.wireOp",EDGE,"E8"),sQuery(id+"F0.wireOp",EDGE,"E35.bottom"),sQuery(id+"F0.wireOp",EDGE,"E35.top"),sQuery(id+"F0.wireOp",EDGE,"E35.left"),sQuery(id+"F0.wireOp",EDGE,"E35.right"),sQuery(id+"F0.wireOp",EDGE,"E36.bottom"),sQuery(id+"F0.wireOp",EDGE,"E36.top"),sQuery(id+"F0.wireOp",EDGE,"E36.left"),sQuery(id+"F0.wireOp",EDGE,"E36.right"),sQuery(id+"F0.wireOp",EDGE,"E37.bottom"),sQuery(id+"F0.wireOp",EDGE,"E37.top"),sQuery(id+"F0.wireOp",EDGE,"E37.left"),sQuery(id+"F0.wireOp",EDGE,"E37.right"),sQuery(id+"F0.wireOp",EDGE,"E38.bottom"),sQuery(id+"F0.wireOp",EDGE,"E38.top"),sQuery(id+"F0.wireOp",EDGE,"E38.left"),sQuery(id+"F0.wireOp",EDGE,"E38.right"),sQuery(id+"F0.wireOp",EDGE,"E39.filletArc"),sQuery(id+"F0.wireOp",EDGE,"E40.filletArc"),sQuery(id+"F0.wireOp",EDGE,"E41.filletArc"),sQuery(id+"F0.wireOp",EDGE,"E42.filletArc"),sQuery(id+"F0.wireOp",EDGE,"E43.0"),sQuery(id+"F0.wireOp",EDGE,"E43.1"),sQuery(id+"F0.wireOp",EDGE,"E43.2"),sQuery(id+"F0.wireOp",EDGE,"E43.3"),sQuery(id+"F0.wireOp",EDGE,"E44.left"),sQuery(id+"F0.wireOp",EDGE,"E44.right"),sQuery(id+"F0.wireOp",EDGE,"E45.left"),sQuery(id+"F0.wireOp",EDGE,"E45.right"),sQuery(id+"F0.wireOp",EDGE,"E46.left"),sQuery(id+"F0.wireOp",EDGE,"E46.right"),sQuery(id+"F0.wireOp",EDGE,"E47.left"),sQuery(id+"F0.wireOp",EDGE,"E47.right"),sQuery(id+"F0.wireOp",EDGE,"E48.left"),sQuery(id+"F0.wireOp",EDGE,"E48.right"),sQuery(id+"F0.wireOp",EDGE,"E49.left"),sQuery(id+"F0.wireOp",EDGE,"E49.right")])]});
            extrude(context, id + "F2", {"entities" : qUnion([Q0, Q1, Q2, Q3, Q4, Q5, Q6, Q7, Q8, Q9, Q10, Q11, Q12, Q13, Q14, Q15, Q16, Q17, Q18, Q19, Q20, Q21, Q22, Q23, Q24, Q25, Q26, Q27, Q28]), "operationType" : NewBodyOperationType.ADD, "oppositeDirection" : true, "endBoundEntityFace" : qUnion([Q29]), "endBoundEntityBody" : qUnion([Q30]), "depth" : 5 * mm});
        }
        {
            var Q0;
            {var subQ6=sQuery(id+"F0.wireOp",EDGE,"E38.left");var subQ11=sQuery(id+"F0.wireOp",EDGE,"E38.top");var subQ13=makeQuery(id+"F0.imprint","INTERSECT",VERTEX,{"derivedFrom":[subQ11,subQ6]});Q0=makeQuery(id+"F0.imprint","IMPRINT",FACE,{"disambiguationData":[TD([[makeQuery(id+"F0.imprint","IMPRINT",EDGE,{"disambiguationData":[TD([[subQ13,-1.0]])],"derivedFrom":subQ11}),1.0]])]});}
            var Q1;
            {var subQ0=sQuery(id+"F0.wireOp",EDGE,"E50.1");Q1=makeQuery(id+"F0.imprint","IMPRINT",FACE,{"disambiguationData":[TD([[makeQuery(id+"F0.imprint","IMPRINT",EDGE,{"derivedFrom":subQ0}),1.0]])]});}
            var Q2;
            {var subQ9=sQuery(id+"F0.wireOp",EDGE,"E35.left");var subQ10=sQuery(id+"F0.wireOp",EDGE,"E35.bottom");var subQ11=makeQuery(id+"F0.imprint","INTERSECT",VERTEX,{"derivedFrom":[subQ10,subQ9]});Q2=makeQuery(id+"F0.imprint","IMPRINT",FACE,{"disambiguationData":[TD([[makeQuery(id+"F0.imprint","IMPRINT",EDGE,{"disambiguationData":[TD([[subQ11,-1.0]])],"derivedFrom":subQ10}),-1.0]])]});}
            var Q3;
            {var subQ0=sQuery(id+"F0.wireOp",EDGE,"E53.1");Q3=makeQuery(id+"F0.imprint","IMPRINT",FACE,{"disambiguationData":[TD([[makeQuery(id+"F0.imprint","IMPRINT",EDGE,{"derivedFrom":subQ0}),1.0]])]});}
            var Q4;
            {var subQ5=sQuery(id+"F0.wireOp",EDGE,"E36.right");var subQ6=sQuery(id+"F0.wireOp",EDGE,"E36.bottom");var subQ7=makeQuery(id+"F0.imprint","INTERSECT",VERTEX,{"derivedFrom":[subQ6,subQ5]});Q4=makeQuery(id+"F0.imprint","IMPRINT",FACE,{"disambiguationData":[TD([[makeQuery(id+"F0.imprint","IMPRINT",EDGE,{"disambiguationData":[TD([[subQ7,1.0]])],"derivedFrom":subQ6}),-1.0]])]});}
            var Q5;
            {var subQ0=sQuery(id+"F0.wireOp",EDGE,"E52.1");Q5=makeQuery(id+"F0.imprint","IMPRINT",FACE,{"disambiguationData":[TD([[makeQuery(id+"F0.imprint","IMPRINT",EDGE,{"derivedFrom":subQ0}),1.0]])]});}
            var Q6;
            {var subQ0=sQuery(id+"F0.wireOp",EDGE,"E51.1");Q6=makeQuery(id+"F0.imprint","IMPRINT",FACE,{"disambiguationData":[TD([[makeQuery(id+"F0.imprint","IMPRINT",EDGE,{"derivedFrom":subQ0}),1.0]])]});}
            var Q7;
            {var subQ5=sQuery(id+"F0.wireOp",EDGE,"E37.left");var subQ6=sQuery(id+"F0.wireOp",EDGE,"E37.top");var subQ7=makeQuery(id+"F0.imprint","INTERSECT",VERTEX,{"derivedFrom":[subQ6,subQ5]});Q7=makeQuery(id+"F0.imprint","IMPRINT",FACE,{"disambiguationData":[TD([[makeQuery(id+"F0.imprint","IMPRINT",EDGE,{"disambiguationData":[TD([[subQ7,-1.0]])],"derivedFrom":subQ6}),-1.0]])]});}
            var Q8;
            {var subQ9=sQuery(id+"F0.wireOp",EDGE,"E70.filletArc");Q8=makeQuery(id+"F0.imprint","IMPRINT",FACE,{"disambiguationData":[TD([[makeQuery(id+"F0.imprint","IMPRINT",EDGE,{"derivedFrom":subQ9}),1.0]])]});}
            var Q9;
            {var subQ9=sQuery(id+"F0.wireOp",EDGE,"E69.filletArc");Q9=makeQuery(id+"F0.imprint","IMPRINT",FACE,{"disambiguationData":[TD([[makeQuery(id+"F0.imprint","IMPRINT",EDGE,{"derivedFrom":subQ9}),1.0]])]});}
            var Q10;
            {var subQ5=sQuery(id+"F0.wireOp",EDGE,"E71.filletArc");Q10=makeQuery(id+"F0.imprint","IMPRINT",FACE,{"disambiguationData":[TD([[makeQuery(id+"F0.imprint","IMPRINT",EDGE,{"derivedFrom":subQ5}),1.0]])]});}
            var Q11;
            {var subQ11=sQuery(id+"F0.wireOp",EDGE,"E68.filletArc");Q11=makeQuery(id+"F0.imprint","IMPRINT",FACE,{"disambiguationData":[TD([[makeQuery(id+"F0.imprint","IMPRINT",EDGE,{"derivedFrom":subQ11}),1.0]])]});}
            extrude(context, id + "F3", {"entities" : qUnion([Q0, Q1, Q2, Q3, Q4, Q5, Q6, Q7, Q8, Q9, Q10, Q11]), "operationType" : NewBodyOperationType.ADD, "oppositeDirection" : true, "depth" : 13 * mm});
        }
        {
            var Q0;
            {var subQ9=sQuery(id+"F0.wireOp",EDGE,"E35.left");var subQ10=sQuery(id+"F0.wireOp",EDGE,"E35.bottom");var subQ11=makeQuery(id+"F0.imprint","INTERSECT",VERTEX,{"derivedFrom":[subQ10,subQ9]});Q0=makeQuery(id+"F0.imprint","IMPRINT",FACE,{"disambiguationData":[TD([[makeQuery(id+"F0.imprint","IMPRINT",EDGE,{"disambiguationData":[TD([[subQ11,-1.0]])],"derivedFrom":subQ10}),-1.0]])]});}
            var Q1;
            {var subQ6=sQuery(id+"F0.wireOp",EDGE,"E0.top");Q1=makeQuery(id+"F0.imprint","IMPRINT",FACE,{"disambiguationData":[TD([[makeQuery(id+"F0.imprint","IMPRINT",EDGE,{"derivedFrom":subQ6}),-1.0]])]});}
            var Q2;
            {var subQ0=sQuery(id+"F0.wireOp",EDGE,"E53.1");Q2=makeQuery(id+"F0.imprint","IMPRINT",FACE,{"disambiguationData":[TD([[makeQuery(id+"F0.imprint","IMPRINT",EDGE,{"derivedFrom":subQ0}),1.0]])]});}
            var Q3;
            {var subQ6=sQuery(id+"F0.wireOp",EDGE,"E0.left");Q3=makeQuery(id+"F0.imprint","IMPRINT",FACE,{"disambiguationData":[TD([[makeQuery(id+"F0.imprint","IMPRINT",EDGE,{"derivedFrom":subQ6}),-1.0]])]});}
            var Q4;
            {var subQ11=sQuery(id+"F0.wireOp",EDGE,"E44.right");Q4=makeQuery(id+"F0.imprint","IMPRINT",FACE,{"disambiguationData":[TD([[makeQuery(id+"F0.imprint","IMPRINT",EDGE,{"derivedFrom":subQ11}),1.0]])]});}
            var Q5;
            {var subQ0=sQuery(id+"F0.wireOp",EDGE,"E52.1");Q5=makeQuery(id+"F0.imprint","IMPRINT",FACE,{"disambiguationData":[TD([[makeQuery(id+"F0.imprint","IMPRINT",EDGE,{"derivedFrom":subQ0}),1.0]])]});}
            var Q6;
            {var subQ5=sQuery(id+"F0.wireOp",EDGE,"E36.right");var subQ6=sQuery(id+"F0.wireOp",EDGE,"E36.bottom");var subQ7=makeQuery(id+"F0.imprint","INTERSECT",VERTEX,{"derivedFrom":[subQ6,subQ5]});Q6=makeQuery(id+"F0.imprint","IMPRINT",FACE,{"disambiguationData":[TD([[makeQuery(id+"F0.imprint","IMPRINT",EDGE,{"disambiguationData":[TD([[subQ7,1.0]])],"derivedFrom":subQ6}),-1.0]])]});}
            var Q7;
            {var subQ0=sQuery(id+"F0.wireOp",EDGE,"E51.1");Q7=makeQuery(id+"F0.imprint","IMPRINT",FACE,{"disambiguationData":[TD([[makeQuery(id+"F0.imprint","IMPRINT",EDGE,{"derivedFrom":subQ0}),1.0]])]});}
            var Q8;
            {var subQ5=sQuery(id+"F0.wireOp",EDGE,"E37.left");var subQ6=sQuery(id+"F0.wireOp",EDGE,"E37.top");var subQ7=makeQuery(id+"F0.imprint","INTERSECT",VERTEX,{"derivedFrom":[subQ6,subQ5]});Q8=makeQuery(id+"F0.imprint","IMPRINT",FACE,{"disambiguationData":[TD([[makeQuery(id+"F0.imprint","IMPRINT",EDGE,{"disambiguationData":[TD([[subQ7,-1.0]])],"derivedFrom":subQ6}),-1.0]])]});}
            var Q9;
            {var subQ6=sQuery(id+"F0.wireOp",EDGE,"E0.bottom");Q9=makeQuery(id+"F0.imprint","IMPRINT",FACE,{"disambiguationData":[TD([[makeQuery(id+"F0.imprint","IMPRINT",EDGE,{"derivedFrom":subQ6}),1.0]])]});}
            var Q10;
            {var subQ0=sQuery(id+"F0.wireOp",EDGE,"E46.bottom");Q10=makeQuery(id+"F0.imprint","IMPRINT",FACE,{"disambiguationData":[TD([[makeQuery(id+"F0.imprint","IMPRINT",EDGE,{"derivedFrom":subQ0}),-1.0]])]});}
            var Q11;
            Q11=makeQuery(id+"F0.imprint","IMPRINT",FACE,{"disambiguationData":[TD([[makeQuery(id+"F0.imprint","IMPRINT",EDGE,{"derivedFrom":sQuery(id+"F0.wireOp",EDGE,"E46.bottom")}),1.0]])]});
            var Q12;
            {var subQ0=sQuery(id+"F0.wireOp",EDGE,"E46.top");Q12=makeQuery(id+"F0.imprint","IMPRINT",FACE,{"disambiguationData":[TD([[makeQuery(id+"F0.imprint","IMPRINT",EDGE,{"derivedFrom":subQ0}),1.0]])]});}
            var Q13;
            Q13=makeQuery(id+"F0.imprint","IMPRINT",FACE,{"disambiguationData":[TD([[makeQuery(id+"F0.imprint","IMPRINT",EDGE,{"derivedFrom":sQuery(id+"F0.wireOp",EDGE,"E47.bottom")}),1.0]])]});
            var Q14;
            {var subQ0=sQuery(id+"F0.wireOp",EDGE,"E47.top");Q14=makeQuery(id+"F0.imprint","IMPRINT",FACE,{"disambiguationData":[TD([[makeQuery(id+"F0.imprint","IMPRINT",EDGE,{"derivedFrom":subQ0}),1.0]])]});}
            var Q15;
            Q15=makeQuery(id+"F0.imprint","IMPRINT",FACE,{"disambiguationData":[TD([[makeQuery(id+"F0.imprint","IMPRINT",EDGE,{"derivedFrom":sQuery(id+"F0.wireOp",EDGE,"E48.bottom")}),1.0]])]});
            var Q16;
            {var subQ0=sQuery(id+"F0.wireOp",EDGE,"E48.top");Q16=makeQuery(id+"F0.imprint","IMPRINT",FACE,{"disambiguationData":[TD([[makeQuery(id+"F0.imprint","IMPRINT",EDGE,{"derivedFrom":subQ0}),1.0]])]});}
            var Q17;
            Q17=makeQuery(id+"F0.imprint","IMPRINT",FACE,{"disambiguationData":[TD([[makeQuery(id+"F0.imprint","IMPRINT",EDGE,{"derivedFrom":sQuery(id+"F0.wireOp",EDGE,"E49.bottom")}),1.0]])]});
            var Q18;
            {var subQ0=sQuery(id+"F0.wireOp",EDGE,"E45.top");Q18=makeQuery(id+"F0.imprint","IMPRINT",FACE,{"disambiguationData":[TD([[makeQuery(id+"F0.imprint","IMPRINT",EDGE,{"derivedFrom":subQ0}),-1.0]])]});}
            var Q19;
            Q19=makeQuery(id+"F0.imprint","IMPRINT",FACE,{"disambiguationData":[TD([[makeQuery(id+"F0.imprint","IMPRINT",EDGE,{"derivedFrom":sQuery(id+"F0.wireOp",EDGE,"E45.bottom")}),-1.0]])]});
            var Q20;
            {var subQ0=sQuery(id+"F0.wireOp",EDGE,"E44.top");Q20=makeQuery(id+"F0.imprint","IMPRINT",FACE,{"disambiguationData":[TD([[makeQuery(id+"F0.imprint","IMPRINT",EDGE,{"derivedFrom":subQ0}),-1.0]])]});}
            var Q21;
            Q21=makeQuery(id+"F0.imprint","IMPRINT",FACE,{"disambiguationData":[TD([[makeQuery(id+"F0.imprint","IMPRINT",EDGE,{"derivedFrom":sQuery(id+"F0.wireOp",EDGE,"E44.bottom")}),-1.0]])]});
            var Q22;
            {var subQ5=sQuery(id+"F0.wireOp",EDGE,"E44.bottom");Q22=makeQuery(id+"F0.imprint","IMPRINT",FACE,{"disambiguationData":[TD([[makeQuery(id+"F0.imprint","IMPRINT",EDGE,{"derivedFrom":subQ5}),1.0]])]});}
            var Q23;
            {var subQ6=sQuery(id+"F0.wireOp",EDGE,"E38.left");var subQ11=sQuery(id+"F0.wireOp",EDGE,"E38.top");var subQ13=makeQuery(id+"F0.imprint","INTERSECT",VERTEX,{"derivedFrom":[subQ11,subQ6]});Q23=makeQuery(id+"F0.imprint","IMPRINT",FACE,{"disambiguationData":[TD([[makeQuery(id+"F0.imprint","IMPRINT",EDGE,{"disambiguationData":[TD([[subQ13,-1.0]])],"derivedFrom":subQ11}),1.0]])]});}
            var Q24;
            {var subQ0=sQuery(id+"F0.wireOp",EDGE,"E50.1");Q24=makeQuery(id+"F0.imprint","IMPRINT",FACE,{"disambiguationData":[TD([[makeQuery(id+"F0.imprint","IMPRINT",EDGE,{"derivedFrom":subQ0}),1.0]])]});}
            var Q25;
            {var subQ4=sQuery(id+"F0.wireOp",EDGE,"E44.left");Q25=makeQuery(id+"F0.imprint","IMPRINT",FACE,{"disambiguationData":[TD([[makeQuery(id+"F0.imprint","IMPRINT",EDGE,{"derivedFrom":subQ4}),1.0]])]});}
            var Q26;
            {var subQ5=sQuery(id+"F0.wireOp",EDGE,"E63.top");Q26=makeQuery(id+"F0.imprint","IMPRINT",FACE,{"disambiguationData":[TD([[makeQuery(id+"F0.imprint","IMPRINT",EDGE,{"derivedFrom":subQ5}),1.0]])]});}
            var Q27;
            Q27=makeQuery(id+"F0.imprint","IMPRINT",FACE,{"disambiguationData":[TD([[makeQuery(id+"F0.imprint","IMPRINT",EDGE,{"derivedFrom":sQuery(id+"F0.wireOp",EDGE,"E63.bottom")}),1.0]])]});
            var Q28;
            Q28=makeQuery(id+"F0.imprint","IMPRINT",FACE,{"disambiguationData":[TD([[makeQuery(id+"F0.imprint","IMPRINT",EDGE,{"derivedFrom":sQuery(id+"F0.wireOp",EDGE,"E62.bottom")}),1.0]])]});
            var Q29;
            Q29=makeQuery(id+"F0.imprint","IMPRINT",FACE,{"disambiguationData":[TD([[makeQuery(id+"F0.imprint","IMPRINT",EDGE,{"derivedFrom":sQuery(id+"F0.wireOp",EDGE,"E61.bottom")}),1.0]])]});
            var Q30;
            Q30=makeQuery(id+"F0.imprint","IMPRINT",FACE,{"disambiguationData":[TD([[makeQuery(id+"F0.imprint","IMPRINT",EDGE,{"derivedFrom":sQuery(id+"F0.wireOp",EDGE,"E60.bottom")}),1.0]])]});
            var Q31;
            Q31=makeQuery(id+"F0.imprint","IMPRINT",FACE,{"disambiguationData":[TD([[makeQuery(id+"F0.imprint","IMPRINT",EDGE,{"derivedFrom":sQuery(id+"F0.wireOp",EDGE,"E59.bottom")}),1.0]])]});
            var Q32;
            Q32=makeQuery(id+"F0.imprint","IMPRINT",FACE,{"disambiguationData":[TD([[makeQuery(id+"F0.imprint","IMPRINT",EDGE,{"derivedFrom":sQuery(id+"F0.wireOp",EDGE,"E58.bottom")}),1.0]])]});
            var Q33;
            {var subQ5=sQuery(id+"F0.wireOp",EDGE,"E58.bottom");Q33=makeQuery(id+"F0.imprint","IMPRINT",FACE,{"disambiguationData":[TD([[makeQuery(id+"F0.imprint","IMPRINT",EDGE,{"derivedFrom":subQ5}),-1.0]])]});}
            var Q34;
            {var subQ5=sQuery(id+"F0.wireOp",EDGE,"E71.filletArc");Q34=makeQuery(id+"F0.imprint","IMPRINT",FACE,{"disambiguationData":[TD([[makeQuery(id+"F0.imprint","IMPRINT",EDGE,{"derivedFrom":subQ5}),1.0]])]});}
            var Q35;
            {var subQ9=sQuery(id+"F0.wireOp",EDGE,"E69.filletArc");Q35=makeQuery(id+"F0.imprint","IMPRINT",FACE,{"disambiguationData":[TD([[makeQuery(id+"F0.imprint","IMPRINT",EDGE,{"derivedFrom":subQ9}),1.0]])]});}
            var Q36;
            {var subQ9=sQuery(id+"F0.wireOp",EDGE,"E70.filletArc");Q36=makeQuery(id+"F0.imprint","IMPRINT",FACE,{"disambiguationData":[TD([[makeQuery(id+"F0.imprint","IMPRINT",EDGE,{"derivedFrom":subQ9}),1.0]])]});}
            var Q37;
            {var subQ11=sQuery(id+"F0.wireOp",EDGE,"E68.filletArc");Q37=makeQuery(id+"F0.imprint","IMPRINT",FACE,{"disambiguationData":[TD([[makeQuery(id+"F0.imprint","IMPRINT",EDGE,{"derivedFrom":subQ11}),1.0]])]});}
            extrude(context, id + "F4", {"entities" : qUnion([Q0, Q1, Q2, Q3, Q4, Q5, Q6, Q7, Q8, Q9, Q10, Q11, Q12, Q13, Q14, Q15, Q16, Q17, Q18, Q19, Q20, Q21, Q22, Q23, Q24, Q25, Q26, Q27, Q28, Q29, Q30, Q31, Q32, Q33, Q34, Q35, Q36, Q37]), "operationType" : NewBodyOperationType.ADD, "depth" : 2 * mm});
        }
    });
